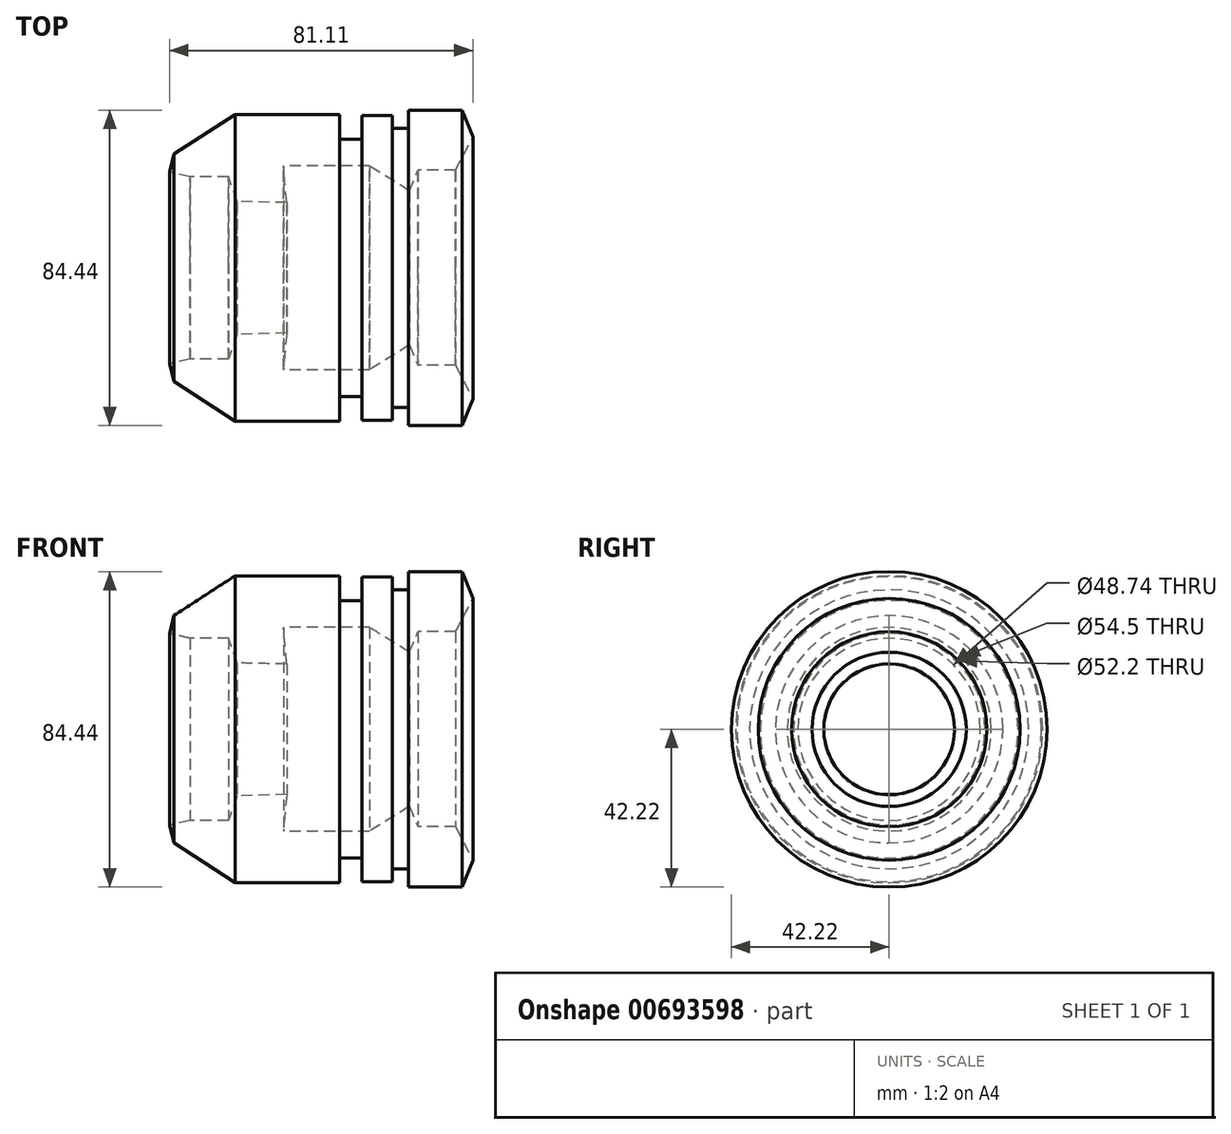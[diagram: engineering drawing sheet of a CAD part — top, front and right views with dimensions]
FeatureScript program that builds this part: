
annotation { "Feature Type Name" : "Feature", "Feature Type Description" : "" }
export const myFeature = defineFeature(function(context is Context, id is Id, definition is map)
    precondition{}
    {
        {
            var Q0;
            Q0=qCreatedBy(makeId("Front.planeOp"),FACE);
            var sketch = newSketch(context, id + "F0", { "sketchPlane" : qUnion([Q0])});
            skLineSegment(sketch, "E0", {"start": v(0, 0) * mm, "end": v(76.7, 0) * mm});
            skLineSegment(sketch, "E1", {"start": v(5.85, 25.6) * mm, "end": v(6.95, 30.42) * mm});
            skLineSegment(sketch, "E2", {"start": v(6.95, 30.42) * mm, "end": v(23.35, 41.06) * mm});
            skLineSegment(sketch, "E3", {"start": v(23.35, 41.06) * mm, "end": v(51.27, 41.06) * mm});
            skLineSegment(sketch, "E4", {"start": v(51.27, 41.06) * mm, "end": v(51.27, 34.45) * mm});
            skLineSegment(sketch, "E5", {"start": v(51.27, 34.45) * mm, "end": v(57.31, 34.45) * mm});
            skLineSegment(sketch, "E6", {"start": v(57.31, 34.45) * mm, "end": v(57.31, 40.78) * mm});
            skLineSegment(sketch, "E7", {"start": v(57.31, 40.78) * mm, "end": v(65.37, 40.78) * mm});
            skLineSegment(sketch, "E8", {"start": v(65.37, 40.78) * mm, "end": v(65.37, 37.32) * mm});
            skLineSegment(sketch, "E9", {"start": v(65.37, 37.32) * mm, "end": v(69.69, 37.32) * mm});
            skLineSegment(sketch, "E10", {"start": v(69.69, 37.32) * mm, "end": v(69.69, 42.22) * mm});
            skLineSegment(sketch, "E11", {"start": v(69.69, 42.22) * mm, "end": v(75.44, 42.22) * mm});
            skLineSegment(sketch, "E12", {"start": v(75.44, 42.22) * mm, "end": v(84.08, 42.22) * mm});
            skLineSegment(sketch, "E13", {"start": v(84.08, 42.22) * mm, "end": v(86.96, 35.02) * mm});
            skLineSegment(sketch, "E14", {"start": v(86.96, 35.02) * mm, "end": v(82.35, 26.1) * mm});
            skLineSegment(sketch, "E15", {"start": v(82.35, 26.1) * mm, "end": v(72.28, 26.1) * mm});
            skLineSegment(sketch, "E16", {"start": v(72.28, 26.1) * mm, "end": v(69.98, 20.63) * mm});
            skLineSegment(sketch, "E17", {"start": v(69.98, 20.63) * mm, "end": v(59.33, 27.25) * mm});
            skLineSegment(sketch, "E18", {"start": v(59.33, 27.25) * mm, "end": v(36.3, 27.25) * mm});
            skLineSegment(sketch, "E19", {"start": v(36.3, 27.25) * mm, "end": v(37.17, 17.46) * mm});
            skLineSegment(sketch, "E20", {"start": v(37.17, 17.46) * mm, "end": v(23.93, 17.75) * mm});
            skLineSegment(sketch, "E21", {"start": v(23.93, 17.75) * mm, "end": v(21.62, 24.37) * mm});
            skLineSegment(sketch, "E22", {"start": v(21.62, 24.37) * mm, "end": v(11.26, 24.37) * mm});
            skLineSegment(sketch, "E23", {"start": v(11.26, 24.37) * mm, "end": v(5.85, 25.6) * mm});
            skSolve(sketch);
        }
        {
            var Q0;
            Q0=makeQuery(id+"F0.imprint","IMPRINT",FACE,{"disambiguationData":[TD([[makeQuery(id+"F0.imprint","IMPRINT",EDGE,{"derivedFrom":sQuery(id+"F0.wireOp",EDGE,"E1")}),-1.0]])]});
            var Q1;
            Q1=sQuery(id+"F0.wireOp",EDGE,"E0");
            revolve(context, id + "F1", {"entities" : qUnion([Q0]), "axis" : qUnion([Q1]), "revolveType" : RevolveType.FULL});
        }
    });
